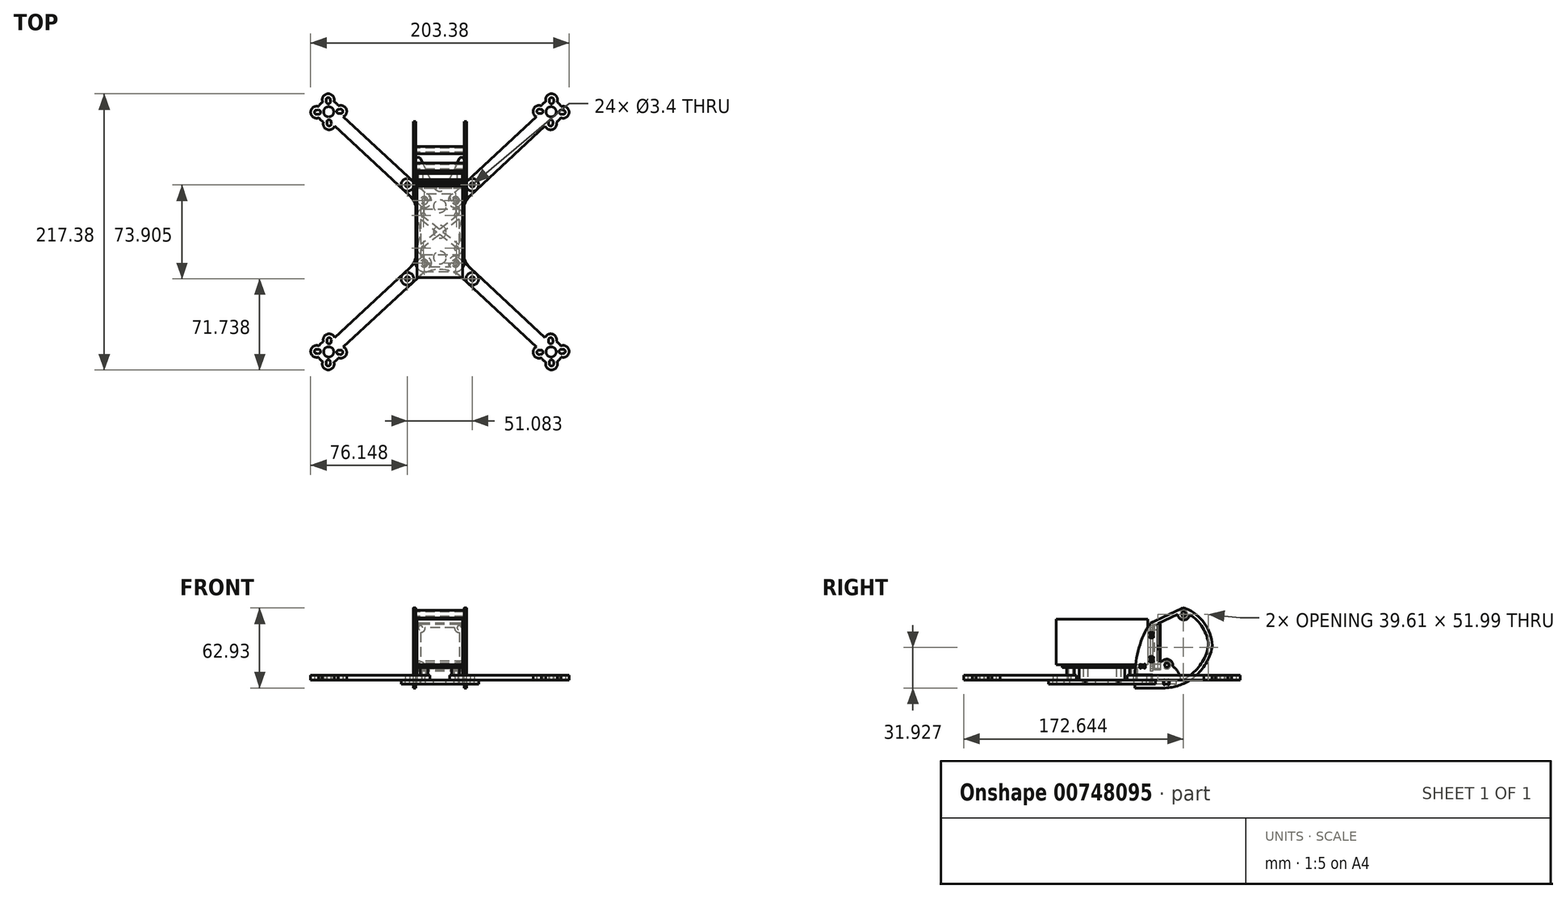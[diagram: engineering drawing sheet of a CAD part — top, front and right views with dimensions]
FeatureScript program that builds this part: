
annotation { "Feature Type Name" : "Feature", "Feature Type Description" : "" }
export const myFeature = defineFeature(function(context is Context, id is Id, definition is map)
    precondition{}
    {
        {
            var Q0;
            Q0=qCreatedBy(makeId("Top.planeOp"),FACE);
            var sketch = newSketch(context, id + "F0", { "sketchPlane" : qUnion([Q0])});
            skCircle(sketch, "E0", {"center": v(-87.5, 94.5) * mm, "radius": 63.5 * mm});
            skCircle(sketch, "E1", {"center": v(87.5, 94.5) * mm, "radius": 63.5 * mm});
            skCircle(sketch, "E2", {"center": v(87.5, -94.5) * mm, "radius": 63.5 * mm});
            skCircle(sketch, "E3", {"center": v(-87.5, -94.5) * mm, "radius": 63.5 * mm});
            skLineSegment(sketch, "E4", {"start": v(-87.5, 94.5) * mm, "end": v(87.5, 94.5) * mm, "construction": true});
            skLineSegment(sketch, "E5", {"start": v(-87.5, 94.5) * mm, "end": v(-87.5, -94.5) * mm, "construction": true});
            skSolve(sketch);
        }
        {
            var Q0;
            Q0=qCreatedBy(makeId("Right.planeOp"),FACE);
            var sketch = newSketch(context, id + "F1", { "sketchPlane" : qUnion([Q0])});
            skLineSegment(sketch, "E6.bottom", {"start": v(36, 41) * mm, "end": v(-36, 41) * mm});
            skLineSegment(sketch, "E6.top", {"start": v(36, 5) * mm, "end": v(-36, 5) * mm});
            skLineSegment(sketch, "E6.left", {"start": v(36, 41) * mm, "end": v(36, 5) * mm});
            skLineSegment(sketch, "E6.right", {"start": v(-36, 41) * mm, "end": v(-36, 5) * mm});
            skSolve(sketch);
        }
        {
            var Q0;
            Q0 = qSketchRegion(id + "F1", true);
            extrude(context, id + "F2", {"entities" : qUnion([Q0]), "endBound" : BoundingType.SYMMETRIC, "depth" : 36 * mm, "offsetDistance" : 25 * mm});
        }
        {
            var Q0;
            Q0=makeQuery(id+"F2.opExtrude","SWEPT_FACE",FACE,{"disambiguationData":[OSD([sQuery(id+"F1.wireOp",EDGE,"E6.left")])]});
            cPlane(context, id + "F3", {"entities" : qUnion([Q0]), "cplaneType" : CPlaneType.OFFSET, "offset" : 2 * mm, "width" : 150 * mm, "height" : 150 * mm});
        }
        {
            var Q0;
            Q0=qCreatedBy(id+"F3.planeOp",FACE);
            var sketch = newSketch(context, id + "F4", { "sketchPlane" : qUnion([Q0])});
            skCircle(sketch, "E7", {"center": v(-15.25, 34.25) * mm, "radius": 1.7 * mm});
            skCircle(sketch, "E8", {"center": v(15.25, 34.25) * mm, "radius": 1.7 * mm});
            skCircle(sketch, "E9", {"center": v(15.25, 3.75) * mm, "radius": 1.7 * mm});
            skCircle(sketch, "E10", {"center": v(-15.25, 3.75) * mm, "radius": 1.7 * mm});
            skLineSegment(sketch, "E11.bottom", {"start": v(-15.25, 37) * mm, "end": v(15.25, 37) * mm, "construction": true});
            skLineSegment(sketch, "E11.top", {"start": v(-15.25, 1) * mm, "end": v(15.25, 1) * mm, "construction": true});
            skLineSegment(sketch, "E11.left", {"start": v(-18, 34.25) * mm, "end": v(-18, 3.75) * mm, "construction": true});
            skLineSegment(sketch, "E11.right", {"start": v(18, 34.25) * mm, "end": v(18, 3.75) * mm, "construction": true});
            skPoint(sketch, "E12.visualSharp", {"position": v(-18, 37) * mm});
            skArc(sketch, "E12.filletArc", {"start": v(-15.25, 37) * mm, "mid": v(-17.2, 36.2) * mm, "end": v(-18, 34.25) * mm, "construction": true});
            skPoint(sketch, "E13.visualSharp", {"position": v(18, 37) * mm});
            skArc(sketch, "E13.filletArc", {"start": v(18, 34.25) * mm, "mid": v(17.2, 36.2) * mm, "end": v(15.25, 37) * mm, "construction": true});
            skPoint(sketch, "E14.visualSharp", {"position": v(18, 1) * mm});
            skArc(sketch, "E14.filletArc", {"start": v(15.25, 1) * mm, "mid": v(17.2, 1.8) * mm, "end": v(18, 3.75) * mm, "construction": true});
            skPoint(sketch, "E15.visualSharp", {"position": v(-18, 1) * mm});
            skArc(sketch, "E15.filletArc", {"start": v(-18, 3.75) * mm, "mid": v(-17.2, 1.8) * mm, "end": v(-15.25, 1) * mm, "construction": true});
            skLineSegment(sketch, "E16.left", {"start": v(-19, 34.25) * mm, "end": v(-19, 31.55) * mm});
            skLineSegment(sketch, "E16.right", {"start": v(19, 34.25) * mm, "end": v(19, 31.55) * mm});
            skLineSegment(sketch, "E17.trimOffspring", {"start": v(-15.25, 0) * mm, "end": v(15.25, 0) * mm});
            skLineSegment(sketch, "E18.trimOffspring", {"start": v(-15.25, 38) * mm, "end": v(15.25, 38) * mm});
            skLineSegment(sketch, "E19.right", {"start": v(15.25, 30.55) * mm, "end": v(15.25, 7.45) * mm});
            skArc(sketch, "E20", {"start": v(-11.55, 34.25) * mm, "mid": v(-12.63, 31.63) * mm, "end": v(-15.25, 30.55) * mm});
            skArc(sketch, "E21", {"start": v(11.55, 34.25) * mm, "mid": v(12.63, 31.63) * mm, "end": v(15.25, 30.55) * mm});
            skArc(sketch, "E22", {"start": v(15.25, 7.45) * mm, "mid": v(12.63, 6.37) * mm, "end": v(11.55, 3.75) * mm});
            skArc(sketch, "E23", {"start": v(-15.25, 7.45) * mm, "mid": v(-12.63, 6.37) * mm, "end": v(-11.55, 3.75) * mm});
            skLineSegment(sketch, "E24.trimOffspring", {"start": v(-11.55, 34.25) * mm, "end": v(11.55, 34.25) * mm});
            skLineSegment(sketch, "E25.trimOffspring", {"start": v(-15.25, 30.55) * mm, "end": v(-15.25, 7.45) * mm});
            skLineSegment(sketch, "E26.trimOffspring", {"start": v(-11.55, 3.75) * mm, "end": v(11.55, 3.75) * mm});
            skArc(sketch, "E27.filletArc", {"start": v(-15.25, 38) * mm, "mid": v(-17.9, 36.9) * mm, "end": v(-19, 34.25) * mm});
            skArc(sketch, "E28.filletArc", {"start": v(19, 34.25) * mm, "mid": v(17.9, 36.9) * mm, "end": v(15.25, 38) * mm});
            skArc(sketch, "E29.filletArc", {"start": v(15.25, 0) * mm, "mid": v(17.9, 1.1) * mm, "end": v(19, 3.75) * mm});
            skArc(sketch, "E30.filletArc", {"start": v(-19, 3.75) * mm, "mid": v(-17.9, 1.1) * mm, "end": v(-15.25, 0) * mm});
            skLineSegment(sketch, "E31.bottom", {"start": v(19, 30.55) * mm, "end": v(21, 30.55) * mm});
            skLineSegment(sketch, "E31.top", {"start": v(19, 26.55) * mm, "end": v(21, 26.55) * mm});
            skLineSegment(sketch, "E31.right", {"start": v(21, 30.55) * mm, "end": v(21, 26.55) * mm});
            skLineSegment(sketch, "E32.bottom", {"start": v(19, 11.45) * mm, "end": v(21, 11.45) * mm});
            skLineSegment(sketch, "E32.top", {"start": v(19, 7.45) * mm, "end": v(21, 7.45) * mm});
            skLineSegment(sketch, "E32.right", {"start": v(21, 11.45) * mm, "end": v(21, 7.45) * mm});
            skLineSegment(sketch, "E33.bottom", {"start": v(-19, 11.45) * mm, "end": v(-21, 11.45) * mm});
            skLineSegment(sketch, "E33.top", {"start": v(-19, 7.45) * mm, "end": v(-21, 7.45) * mm});
            skLineSegment(sketch, "E33.right", {"start": v(-21, 11.45) * mm, "end": v(-21, 7.45) * mm});
            skLineSegment(sketch, "E34.bottom", {"start": v(-19, 26.55) * mm, "end": v(-21, 26.55) * mm});
            skLineSegment(sketch, "E34.top", {"start": v(-19, 30.55) * mm, "end": v(-21, 30.55) * mm});
            skLineSegment(sketch, "E34.right", {"start": v(-21, 26.55) * mm, "end": v(-21, 30.55) * mm});
            skArc(sketch, "E35", {"start": v(-19, 30.55) * mm, "mid": v(-18.5, 31.05) * mm, "end": v(-19, 31.55) * mm});
            skArc(sketch, "E36", {"start": v(-19, 26.55) * mm, "mid": v(-18.5, 26.05) * mm, "end": v(-19, 25.55) * mm});
            skArc(sketch, "E37", {"start": v(19, 30.55) * mm, "mid": v(18.5, 31.05) * mm, "end": v(19, 31.55) * mm});
            skArc(sketch, "E38", {"start": v(19, 26.55) * mm, "mid": v(18.5, 26.05) * mm, "end": v(19, 25.55) * mm});
            skLineSegment(sketch, "E39.trimOffspring", {"start": v(-19, 25.55) * mm, "end": v(-19, 12.45) * mm});
            skLineSegment(sketch, "E40.trimOffspring", {"start": v(19, 25.55) * mm, "end": v(19, 12.45) * mm});
            skArc(sketch, "E41", {"start": v(-19, 11.45) * mm, "mid": v(-18.5, 11.95) * mm, "end": v(-19, 12.45) * mm});
            skArc(sketch, "E42", {"start": v(-19, 7.45) * mm, "mid": v(-18.5, 6.95) * mm, "end": v(-19, 6.45) * mm});
            skLineSegment(sketch, "E43.trimOffspring", {"start": v(-19, 6.45) * mm, "end": v(-19, 3.75) * mm});
            skArc(sketch, "E44", {"start": v(19, 11.45) * mm, "mid": v(18.5, 11.95) * mm, "end": v(19, 12.45) * mm});
            skArc(sketch, "E45", {"start": v(19, 7.45) * mm, "mid": v(18.5, 6.95) * mm, "end": v(19, 6.45) * mm});
            skLineSegment(sketch, "E46.trimOffspring", {"start": v(19, 6.45) * mm, "end": v(19, 3.75) * mm});
            skSolve(sketch);
        }
        {
            var Q0;
            Q0 = qSketchRegion(id + "F4", true);
            extrude(context, id + "F5", {"entities" : qUnion([Q0]), "depth" : 2 * mm, "offsetDistance" : 25 * mm});
        }
        {
            var Q0;
            Q0=makeQuery(id+"F5.opExtrude","CAP_FACE",FACE,{"disambiguationData":[OSD([sQuery(id+"F4.wireOp",EDGE,"E7"),sQuery(id+"F4.wireOp",EDGE,"E8"),sQuery(id+"F4.wireOp",EDGE,"E9"),sQuery(id+"F4.wireOp",EDGE,"E10"),sQuery(id+"F4.wireOp",EDGE,"E16.bottom"),sQuery(id+"F4.wireOp",EDGE,"E16.top"),sQuery(id+"F4.wireOp",EDGE,"E16.left"),sQuery(id+"F4.wireOp",EDGE,"E16.right"),sQuery(id+"F4.wireOp",EDGE,"0tjX9AGm-dfaZ-di7K-9Cjz-SUyM1mQiOhD7.top"),sQuery(id+"F4.wireOp",EDGE,"0tjX9AGm-dfaZ-di7K-9Cjz-SUyM1mQiOhD7.left"),sQuery(id+"F4.wireOp",EDGE,"0tjX9AGm-dfaZ-di7K-9Cjz-SUyM1mQiOhD7.right"),sQuery(id+"F4.wireOp",EDGE,"jNbVTTfh-dDnQ-iOIQ-lGc2-BmaGoyWdqRNK.top"),sQuery(id+"F4.wireOp",EDGE,"jNbVTTfh-dDnQ-iOIQ-lGc2-BmaGoyWdqRNK.left"),sQuery(id+"F4.wireOp",EDGE,"jNbVTTfh-dDnQ-iOIQ-lGc2-BmaGoyWdqRNK.right"),sQuery(id+"F4.wireOp",EDGE,"p8So4zwG-Bp0h-plD2-JnCm-BeE0CadOh8gG.top"),sQuery(id+"F4.wireOp",EDGE,"p8So4zwG-Bp0h-plD2-JnCm-BeE0CadOh8gG.left"),sQuery(id+"F4.wireOp",EDGE,"p8So4zwG-Bp0h-plD2-JnCm-BeE0CadOh8gG.right"),sQuery(id+"F4.wireOp",EDGE,"Rqj2pUDk-Wo8M-VqOy-AQv9-rM1yGNZkRYXT.top"),sQuery(id+"F4.wireOp",EDGE,"Rqj2pUDk-Wo8M-VqOy-AQv9-rM1yGNZkRYXT.left"),sQuery(id+"F4.wireOp",EDGE,"Rqj2pUDk-Wo8M-VqOy-AQv9-rM1yGNZkRYXT.right"),sQuery(id+"F4.wireOp",EDGE,"cf8581b7-b0b2-420e-8d79-318895d83493.trimOffspring"),sQuery(id+"F4.wireOp",EDGE,"E17.trimOffspring"),sQuery(id+"F4.wireOp",EDGE,"E18.trimOffspring"),sQuery(id+"F4.wireOp",EDGE,"2b6bb1a9-3bb7-41ad-b322-06cd7e0aa122.trimOffspring"),sQuery(id+"F4.wireOp",EDGE,"E19.right"),sQuery(id+"F4.wireOp",EDGE,"E20"),sQuery(id+"F4.wireOp",EDGE,"E21"),sQuery(id+"F4.wireOp",EDGE,"E22"),sQuery(id+"F4.wireOp",EDGE,"E23"),sQuery(id+"F4.wireOp",EDGE,"E24.trimOffspring"),sQuery(id+"F4.wireOp",EDGE,"E25.trimOffspring"),sQuery(id+"F4.wireOp",EDGE,"E26.trimOffspring"),sQuery(id+"F4.wireOp",EDGE,"E27.filletArc"),sQuery(id+"F4.wireOp",EDGE,"E28.filletArc"),sQuery(id+"F4.wireOp",EDGE,"E29.filletArc"),sQuery(id+"F4.wireOp",EDGE,"E30.filletArc")])],"isStart":false});
            cPlane(context, id + "F6", {"entities" : qUnion([Q0]), "cplaneType" : CPlaneType.OFFSET, "offset" : 1 * mm, "width" : 150 * mm, "height" : 150 * mm});
        }
        {
            var Q0;
            Q0=qCreatedBy(id+"F6.planeOp",FACE);
            var sketch = newSketch(context, id + "F7", { "sketchPlane" : qUnion([Q0])});
            skCircle(sketch, "E47", {"center": v(-15.25, 34.25) * mm, "radius": 1.7 * mm});
            skCircle(sketch, "E48", {"center": v(15.25, 34.25) * mm, "radius": 1.7 * mm});
            skCircle(sketch, "E49", {"center": v(15.25, 3.75) * mm, "radius": 1.7 * mm});
            skCircle(sketch, "E50", {"center": v(-15.25, 3.75) * mm, "radius": 1.7 * mm});
            skLineSegment(sketch, "E51.bottom", {"start": v(-15.25, 37) * mm, "end": v(15.25, 37) * mm});
            skLineSegment(sketch, "E51.top", {"start": v(-15.25, 1) * mm, "end": v(15.25, 1) * mm});
            skLineSegment(sketch, "E51.left", {"start": v(-18, 34.25) * mm, "end": v(-18, 3.75) * mm});
            skLineSegment(sketch, "E51.right", {"start": v(18, 34.25) * mm, "end": v(18, 3.75) * mm});
            skPoint(sketch, "E52.visualSharp", {"position": v(-18, 37) * mm});
            skArc(sketch, "E52.filletArc", {"start": v(-15.25, 37) * mm, "mid": v(-17.2, 36.2) * mm, "end": v(-18, 34.25) * mm});
            skPoint(sketch, "E53.visualSharp", {"position": v(18, 37) * mm});
            skArc(sketch, "E53.filletArc", {"start": v(18, 34.25) * mm, "mid": v(17.2, 36.2) * mm, "end": v(15.25, 37) * mm});
            skPoint(sketch, "E54.visualSharp", {"position": v(18, 1) * mm});
            skArc(sketch, "E54.filletArc", {"start": v(15.25, 1) * mm, "mid": v(17.2, 1.8) * mm, "end": v(18, 3.75) * mm});
            skPoint(sketch, "E55.visualSharp", {"position": v(-18, 1) * mm});
            skArc(sketch, "E55.filletArc", {"start": v(-18, 3.75) * mm, "mid": v(-17.2, 1.8) * mm, "end": v(-15.25, 1) * mm});
            skSolve(sketch);
        }
        {
            var Q0;
            Q0 = qSketchRegion(id + "F7", true);
            extrude(context, id + "F8", {"entities" : qUnion([Q0]), "depth" : 5 * mm, "offsetDistance" : 25 * mm});
        }
        {
            var Q0;
            Q0=qCreatedBy(makeId("Right.planeOp"),FACE);
            cPlane(context, id + "F9", {"entities" : qUnion([Q0]), "cplaneType" : CPlaneType.OFFSET, "offset" : 19 * mm, "oppositeDirection" : true, "width" : 150 * mm, "height" : 150 * mm});
        }
        {
            var Q0;
            Q0=qCreatedBy(makeId("Top.planeOp"),FACE);
            cPlane(context, id + "F10", {"entities" : qUnion([Q0]), "cplaneType" : CPlaneType.OFFSET, "offset" : 3 * mm, "oppositeDirection" : true, "width" : 150 * mm, "height" : 150 * mm});
        }
        {
            var Q0;
            Q0=qCreatedBy(id+"F10.planeOp",FACE);
            var sketch = newSketch(context, id + "F11", { "sketchPlane" : qUnion([Q0])});
            skLineSegment(sketch, "E56.bottom", {"start": v(-22.09, 35.9) * mm, "end": v(22.09, 35.9) * mm});
            skLineSegment(sketch, "E56.top", {"start": v(-22.09, -35.74) * mm, "end": v(22.09, -35.74) * mm});
            skLineSegment(sketch, "E56.left", {"start": v(-22.09, 35.9) * mm, "end": v(-22.09, -35.74) * mm});
            skLineSegment(sketch, "E56.right", {"start": v(22.09, 35.9) * mm, "end": v(22.09, -35.74) * mm});
            skLineSegment(sketch, "E57.bottom", {"start": v(-16.09, 32.9) * mm, "end": v(16.09, 32.9) * mm});
            skLineSegment(sketch, "E57.top", {"start": v(-16.09, -32.74) * mm, "end": v(16.09, -32.74) * mm});
            skLineSegment(sketch, "E57.left", {"start": v(-19.09, 29.9) * mm, "end": v(-19.09, -29.74) * mm});
            skLineSegment(sketch, "E57.right", {"start": v(19.09, 29.9) * mm, "end": v(19.09, -29.74) * mm});
            skPoint(sketch, "E58.visualSharp", {"position": v(-19.09, 32.9) * mm});
            skArc(sketch, "E58.filletArc", {"start": v(-16.09, 32.9) * mm, "mid": v(-18.2, 32.02) * mm, "end": v(-19.09, 29.9) * mm});
            skPoint(sketch, "E59.visualSharp", {"position": v(19.09, 32.9) * mm});
            skArc(sketch, "E59.filletArc", {"start": v(19.09, 29.9) * mm, "mid": v(18.2, 32.02) * mm, "end": v(16.09, 32.9) * mm});
            skPoint(sketch, "E60.visualSharp", {"position": v(19.09, -32.74) * mm});
            skArc(sketch, "E60.filletArc", {"start": v(16.09, -32.74) * mm, "mid": v(18.2, -31.86) * mm, "end": v(19.09, -29.74) * mm});
            skPoint(sketch, "E61.visualSharp", {"position": v(-19.09, -32.74) * mm});
            skArc(sketch, "E61.filletArc", {"start": v(-19.09, -29.74) * mm, "mid": v(-18.2, -31.86) * mm, "end": v(-16.09, -32.74) * mm});
            skLineSegment(sketch, "E62.bottom", {"start": v(-18, 18) * mm, "end": v(18, 18) * mm, "construction": true});
            skLineSegment(sketch, "E62.top", {"start": v(-18, -18) * mm, "end": v(18, -18) * mm, "construction": true});
            skLineSegment(sketch, "E62.left", {"start": v(-18, 18) * mm, "end": v(-18, -18) * mm, "construction": true});
            skLineSegment(sketch, "E62.right", {"start": v(18, 18) * mm, "end": v(18, -18) * mm, "construction": true});
            skCircle(sketch, "E63", {"center": v(-25.54, 36.95) * mm, "radius": 1.7 * mm});
            skCircle(sketch, "E64", {"center": v(25.54, 36.95) * mm, "radius": 1.7 * mm});
            skCircle(sketch, "E65", {"center": v(-25.54, -36.95) * mm, "radius": 1.7 * mm});
            skCircle(sketch, "E66", {"center": v(25.54, -36.95) * mm, "radius": 1.7 * mm});
            skLineSegment(sketch, "E67", {"start": v(-87.5, 94.5) * mm, "end": v(-12.35, 24.7) * mm, "construction": true});
            skCircle(sketch, "E68.cCircle", {"center": v(-25.54, 36.95) * mm, "radius": 2.6 * mm, "construction": true});
            skLineSegment(sketch, "E68.0", {"start": v(-27.04, 39.55) * mm, "end": v(-24.04, 39.55) * mm, "construction": true});
            skLineSegment(sketch, "E68.1", {"start": v(-24.04, 39.55) * mm, "end": v(-22.54, 36.95) * mm, "construction": true});
            skLineSegment(sketch, "E68.2", {"start": v(-22.54, 36.95) * mm, "end": v(-24.04, 34.35) * mm, "construction": true});
            skLineSegment(sketch, "E68.3", {"start": v(-24.04, 34.35) * mm, "end": v(-27.04, 34.35) * mm, "construction": true});
            skLineSegment(sketch, "E68.4", {"start": v(-27.04, 34.35) * mm, "end": v(-28.54, 36.95) * mm, "construction": true});
            skLineSegment(sketch, "E68.5", {"start": v(-28.54, 36.95) * mm, "end": v(-27.04, 39.55) * mm, "construction": true});
            skPoint(sketch, "E68.0.midPoint", {"position": v(-25.54, 39.55) * mm});
            skCircle(sketch, "E69", {"center": v(-12.35, 24.7) * mm, "radius": 1.7 * mm, "construction": true});
            skCircle(sketch, "E70.cCircle", {"center": v(-12.35, 24.7) * mm, "radius": 2.6 * mm, "construction": true});
            skLineSegment(sketch, "E70.0", {"start": v(-12.35, 27.7) * mm, "end": v(-9.75, 26.2) * mm});
            skLineSegment(sketch, "E70.1", {"start": v(-9.75, 26.2) * mm, "end": v(-9.75, 23.2) * mm});
            skLineSegment(sketch, "E70.2", {"start": v(-9.75, 23.2) * mm, "end": v(-12.35, 21.7) * mm});
            skLineSegment(sketch, "E70.3", {"start": v(-12.35, 21.7) * mm, "end": v(-14.95, 23.2) * mm});
            skLineSegment(sketch, "E70.4", {"start": v(-14.95, 23.2) * mm, "end": v(-14.95, 26.2) * mm});
            skLineSegment(sketch, "E70.5", {"start": v(-14.95, 26.2) * mm, "end": v(-12.35, 27.7) * mm});
            skPoint(sketch, "E70.0.midPoint", {"position": v(-11.05, 26.95) * mm});
            skSolve(sketch);
        }
        {
            var Q0;
            Q0=qCreatedBy(id+"F10.planeOp",FACE);
            cPlane(context, id + "F12", {"entities" : qUnion([Q0]), "cplaneType" : CPlaneType.OFFSET, "offset" : 4 * mm, "oppositeDirection" : true, "width" : 150 * mm, "height" : 150 * mm});
        }
        {
            var Q0;
            Q0=qCreatedBy(id+"F12.planeOp",FACE);
            var sketch = newSketch(context, id + "F13", { "sketchPlane" : qUnion([Q0])});
            skCircle(sketch, "E71", {"center": v(-25.54, 36.95) * mm, "radius": 1.7 * mm});
            skArc(sketch, "E72", {"start": v(-11.2, 25.95) * mm, "mid": v(-13.6, 25.86) * mm, "end": v(-13.5, 23.46) * mm});
            skLineSegment(sketch, "E73", {"start": v(-75.97, 90.61) * mm, "end": v(-7.83, 27.33) * mm});
            skLineSegment(sketch, "E74", {"start": v(-14.64, 20) * mm, "end": v(-82.78, 83.29) * mm});
            skLineSegment(sketch, "E75", {"start": v(-11.2, 25.95) * mm, "end": v(-9.95, 24.8) * mm});
            skLineSegment(sketch, "E76", {"start": v(-13.5, 23.46) * mm, "end": v(-12.26, 22.3) * mm});
            skLineSegment(sketch, "E77", {"start": v(-7.83, 27.33) * mm, "end": v(-8.3, 25.3) * mm});
            skLineSegment(sketch, "E78", {"start": v(-12.65, 20.61) * mm, "end": v(-14.64, 20) * mm});
            skPoint(sketch, "E79.visualSharp", {"position": v(-11, 21.12) * mm});
            skArc(sketch, "E79.filletArc", {"start": v(-12.65, 20.61) * mm, "mid": v(-11.97, 21.34) * mm, "end": v(-12.26, 22.3) * mm});
            skPoint(sketch, "E80.visualSharp", {"position": v(-8.68, 23.61) * mm});
            skArc(sketch, "E80.filletArc", {"start": v(-9.95, 24.8) * mm, "mid": v(-8.98, 24.57) * mm, "end": v(-8.3, 25.3) * mm});
            skCircle(sketch, "E81", {"center": v(-87.5, 94.5) * mm, "radius": 4 * mm});
            skArc(sketch, "E82", {"start": v(-88.85, 84.94) * mm, "mid": v(-87.09, 83.3) * mm, "end": v(-85.45, 85.07) * mm});
            skLineSegment(sketch, "E83", {"start": v(-87.15, 85) * mm, "end": v(-87.85, 104) * mm, "construction": true});
            skLineSegment(sketch, "E84", {"start": v(-89.55, 103.93) * mm, "end": v(-89.5, 102.43) * mm});
            skLineSegment(sketch, "E85.trimOffspring", {"start": v(-85.5, 86.57) * mm, "end": v(-85.45, 85.07) * mm});
            skLineSegment(sketch, "E86.trimOffspring", {"start": v(-88.9, 86.44) * mm, "end": v(-88.85, 84.94) * mm});
            skLineSegment(sketch, "E87", {"start": v(-86.1, 102.56) * mm, "end": v(-86.15, 104.06) * mm});
            skLineSegment(sketch, "E88", {"start": v(-97.06, 95.85) * mm, "end": v(-95.56, 95.9) * mm});
            skLineSegment(sketch, "E89", {"start": v(-77.94, 93.15) * mm, "end": v(-79.44, 93.1) * mm});
            skLineSegment(sketch, "E90.trimOffspring", {"start": v(-95.43, 92.5) * mm, "end": v(-96.93, 92.45) * mm});
            skLineSegment(sketch, "E91.trimOffspring", {"start": v(-79.57, 96.5) * mm, "end": v(-78.07, 96.55) * mm});
            skLineSegment(sketch, "E92", {"start": v(-97, 94.15) * mm, "end": v(-78, 94.85) * mm, "construction": true});
            skArc(sketch, "E93", {"start": v(-95.5, 98.6) * mm, "mid": v(-101.7, 93.98) * mm, "end": v(-95.17, 89.82) * mm});
            skArc(sketch, "E94", {"start": v(-92.18, 102.17) * mm, "mid": v(-88.02, 108.7) * mm, "end": v(-83.4, 102.5) * mm});
            skArc(sketch, "E95", {"start": v(-79.83, 99.18) * mm, "mid": v(-73.3, 95.02) * mm, "end": v(-79.5, 90.4) * mm});
            skArc(sketch, "E96", {"start": v(-91.6, 86.5) * mm, "mid": v(-86.98, 80.3) * mm, "end": v(-82.82, 86.83) * mm});
            skArc(sketch, "E97.trimOffspring", {"start": v(-95.17, 89.82) * mm, "mid": v(-93.62, 87.92) * mm, "end": v(-91.6, 86.5) * mm});
            skArc(sketch, "E98.trimOffspring", {"start": v(-95.43, 92.5) * mm, "mid": v(-93.8, 94.27) * mm, "end": v(-95.56, 95.9) * mm});
            skArc(sketch, "E99.trimOffspring", {"start": v(-97.06, 95.85) * mm, "mid": v(-98.7, 94.09) * mm, "end": v(-96.93, 92.45) * mm});
            skArc(sketch, "E100.trimOffspring", {"start": v(-89.5, 102.43) * mm, "mid": v(-87.73, 100.8) * mm, "end": v(-86.1, 102.56) * mm});
            skArc(sketch, "E101.trimOffspring", {"start": v(-86.15, 104.06) * mm, "mid": v(-87.91, 105.7) * mm, "end": v(-89.55, 103.93) * mm});
            skArc(sketch, "E102.trimOffspring", {"start": v(-92.18, 102.17) * mm, "mid": v(-94.08, 100.62) * mm, "end": v(-95.5, 98.6) * mm});
            skArc(sketch, "E103.trimOffspring", {"start": v(-79.83, 99.18) * mm, "mid": v(-81.38, 101.08) * mm, "end": v(-83.4, 102.5) * mm});
            skArc(sketch, "E104.trimOffspring", {"start": v(-77.94, 93.15) * mm, "mid": v(-76.3, 94.91) * mm, "end": v(-78.07, 96.55) * mm});
            skArc(sketch, "E105.trimOffspring", {"start": v(-79.57, 96.5) * mm, "mid": v(-81.2, 94.73) * mm, "end": v(-79.44, 93.1) * mm});
            skArc(sketch, "E106.trimOffspring", {"start": v(-82.82, 86.83) * mm, "mid": v(-80.92, 88.38) * mm, "end": v(-79.5, 90.4) * mm});
            skArc(sketch, "E107.trimOffspring", {"start": v(-85.5, 86.57) * mm, "mid": v(-87.27, 88.2) * mm, "end": v(-88.9, 86.44) * mm});
            skLineSegment(sketch, "E108", {"start": v(-12.35, 24.7) * mm, "end": v(-87.5, 94.5) * mm, "construction": true});
            skArc(sketch, "E109.MirrorCS", {"start": v(86.15, 104.06) * mm, "mid": v(87.91, 105.7) * mm, "end": v(89.55, 103.93) * mm});
            skLineSegment(sketch, "E110.MirrorCS", {"start": v(79.57, 96.5) * mm, "end": v(78.07, 96.55) * mm});
            skArc(sketch, "E111.MirrorCS", {"start": v(79.57, 96.5) * mm, "mid": v(81.2, 94.73) * mm, "end": v(79.44, 93.1) * mm});
            skLineSegment(sketch, "E112.MirrorCS", {"start": v(7.83, 27.33) * mm, "end": v(8.3, 25.3) * mm});
            skLineSegment(sketch, "E113.MirrorCS", {"start": v(86.1, 102.56) * mm, "end": v(86.15, 104.06) * mm});
            skArc(sketch, "E114.MirrorCS", {"start": v(88.85, 84.94) * mm, "mid": v(87.09, 83.3) * mm, "end": v(85.45, 85.07) * mm});
            skLineSegment(sketch, "E115.MirrorCS", {"start": v(97.06, 95.85) * mm, "end": v(95.56, 95.9) * mm});
            skArc(sketch, "E116.MirrorCS", {"start": v(89.5, 102.43) * mm, "mid": v(87.73, 100.8) * mm, "end": v(86.1, 102.56) * mm});
            skArc(sketch, "E117.MirrorCS", {"start": v(97.06, 95.85) * mm, "mid": v(98.7, 94.09) * mm, "end": v(96.93, 92.45) * mm});
            skLineSegment(sketch, "E118.MirrorCS", {"start": v(12.65, 20.61) * mm, "end": v(14.64, 20) * mm});
            skLineSegment(sketch, "E119.MirrorCS", {"start": v(89.55, 103.93) * mm, "end": v(89.5, 102.43) * mm});
            skLineSegment(sketch, "E120.MirrorCS", {"start": v(95.43, 92.5) * mm, "end": v(96.93, 92.45) * mm});
            skArc(sketch, "E121.MirrorCS", {"start": v(12.65, 20.61) * mm, "mid": v(11.97, 21.34) * mm, "end": v(12.26, 22.3) * mm});
            skLineSegment(sketch, "E122.MirrorCS", {"start": v(77.94, 93.15) * mm, "end": v(79.44, 93.1) * mm});
            skLineSegment(sketch, "E123.MirrorCS", {"start": v(85.5, 86.57) * mm, "end": v(85.45, 85.07) * mm});
            skArc(sketch, "E124.MirrorCS", {"start": v(9.95, 24.8) * mm, "mid": v(8.98, 24.57) * mm, "end": v(8.3, 25.3) * mm});
            skLineSegment(sketch, "E125.MirrorCS", {"start": v(88.9, 86.44) * mm, "end": v(88.85, 84.94) * mm});
            skLineSegment(sketch, "E126.MirrorCS", {"start": v(13.5, 23.46) * mm, "end": v(12.26, 22.3) * mm});
            skArc(sketch, "E127.MirrorCS", {"start": v(95.43, 92.5) * mm, "mid": v(93.8, 94.27) * mm, "end": v(95.56, 95.9) * mm});
            skLineSegment(sketch, "E128.MirrorCS", {"start": v(11.2, 25.95) * mm, "end": v(9.95, 24.8) * mm});
            skArc(sketch, "E129.MirrorCS", {"start": v(77.94, 93.15) * mm, "mid": v(76.3, 94.91) * mm, "end": v(78.07, 96.55) * mm});
            skArc(sketch, "E130.MirrorCS", {"start": v(11.2, 25.95) * mm, "mid": v(13.6, 25.86) * mm, "end": v(13.5, 23.46) * mm});
            skArc(sketch, "E131.MirrorCS", {"start": v(85.5, 86.57) * mm, "mid": v(87.27, 88.2) * mm, "end": v(88.9, 86.44) * mm});
            skArc(sketch, "E132.MirrorCS", {"start": v(82.82, 86.83) * mm, "mid": v(80.92, 88.38) * mm, "end": v(79.5, 90.4) * mm});
            skLineSegment(sketch, "E133.MirrorCS", {"start": v(87.15, 85) * mm, "end": v(87.85, 104) * mm, "construction": true});
            skArc(sketch, "E134.MirrorCS", {"start": v(79.83, 99.18) * mm, "mid": v(81.38, 101.08) * mm, "end": v(83.4, 102.5) * mm});
            skArc(sketch, "E135.MirrorCS", {"start": v(95.17, 89.82) * mm, "mid": v(93.62, 87.92) * mm, "end": v(91.6, 86.5) * mm});
            skArc(sketch, "E136.MirrorCS", {"start": v(92.18, 102.17) * mm, "mid": v(94.08, 100.62) * mm, "end": v(95.5, 98.6) * mm});
            skLineSegment(sketch, "E137.MirrorCS", {"start": v(12.35, 24.7) * mm, "end": v(87.5, 94.5) * mm, "construction": true});
            skLineSegment(sketch, "E138.MirrorCS", {"start": v(97, 94.15) * mm, "end": v(78, 94.85) * mm, "construction": true});
            skArc(sketch, "E139.MirrorCS", {"start": v(91.6, 86.5) * mm, "mid": v(86.98, 80.3) * mm, "end": v(82.82, 86.83) * mm});
            skCircle(sketch, "E140.MirrorC", {"center": v(25.54, 36.95) * mm, "radius": 1.7 * mm});
            skCircle(sketch, "E141.MirrorC", {"center": v(87.5, 94.5) * mm, "radius": 4 * mm});
            skLineSegment(sketch, "E142.MirrorCS", {"start": v(75.97, 90.61) * mm, "end": v(7.83, 27.33) * mm});
            skLineSegment(sketch, "E143.MirrorCS", {"start": v(14.64, 20) * mm, "end": v(82.78, 83.29) * mm});
            skArc(sketch, "E144.MirrorCS", {"start": v(92.18, 102.17) * mm, "mid": v(88.02, 108.7) * mm, "end": v(83.4, 102.5) * mm});
            skArc(sketch, "E145.MirrorCS", {"start": v(79.83, 99.18) * mm, "mid": v(73.3, 95.02) * mm, "end": v(79.5, 90.4) * mm});
            skPoint(sketch, "E146.MirrorP", {"position": v(11, 21.12) * mm});
            skArc(sketch, "E147.MirrorCS", {"start": v(95.5, 98.6) * mm, "mid": v(101.7, 93.98) * mm, "end": v(95.17, 89.82) * mm});
            skPoint(sketch, "E148.MirrorP", {"position": v(8.68, 23.61) * mm});
            skLineSegment(sketch, "E149.MirrorCS", {"start": v(95.43, -92.5) * mm, "end": v(96.93, -92.45) * mm});
            skArc(sketch, "E150.MirrorCS", {"start": v(97.06, -95.85) * mm, "mid": v(98.7, -94.09) * mm, "end": v(96.93, -92.45) * mm});
            skLineSegment(sketch, "E151.MirrorCS", {"start": v(97.06, -95.85) * mm, "end": v(95.56, -95.9) * mm});
            skLineSegment(sketch, "E152.MirrorCS", {"start": v(88.9, -86.44) * mm, "end": v(88.85, -84.94) * mm});
            skLineSegment(sketch, "E153.MirrorCS", {"start": v(11.2, -25.95) * mm, "end": v(9.95, -24.8) * mm});
            skLineSegment(sketch, "E154.MirrorCS", {"start": v(7.83, -27.33) * mm, "end": v(8.3, -25.3) * mm});
            skArc(sketch, "E155.MirrorCS", {"start": v(9.95, -24.8) * mm, "mid": v(8.98, -24.57) * mm, "end": v(8.3, -25.3) * mm});
            skArc(sketch, "E156.MirrorCS", {"start": v(88.85, -84.94) * mm, "mid": v(87.09, -83.3) * mm, "end": v(85.45, -85.07) * mm});
            skLineSegment(sketch, "E157.MirrorCS", {"start": v(-11.2, -25.95) * mm, "end": v(-9.95, -24.8) * mm});
            skLineSegment(sketch, "E158.MirrorCS", {"start": v(-88.9, -86.44) * mm, "end": v(-88.85, -84.94) * mm});
            skArc(sketch, "E159.MirrorCS", {"start": v(-77.94, -93.15) * mm, "mid": v(-76.3, -94.91) * mm, "end": v(-78.07, -96.55) * mm});
            skLineSegment(sketch, "E160.MirrorCS", {"start": v(85.5, -86.57) * mm, "end": v(85.45, -85.07) * mm});
            skLineSegment(sketch, "E161.MirrorCS", {"start": v(-7.83, -27.33) * mm, "end": v(-8.3, -25.3) * mm});
            skArc(sketch, "E162.MirrorCS", {"start": v(-9.95, -24.8) * mm, "mid": v(-8.98, -24.57) * mm, "end": v(-8.3, -25.3) * mm});
            skLineSegment(sketch, "E163.MirrorCS", {"start": v(-85.5, -86.57) * mm, "end": v(-85.45, -85.07) * mm});
            skArc(sketch, "E164.MirrorCS", {"start": v(-88.85, -84.94) * mm, "mid": v(-87.09, -83.3) * mm, "end": v(-85.45, -85.07) * mm});
            skLineSegment(sketch, "E165.MirrorCS", {"start": v(-77.94, -93.15) * mm, "end": v(-79.44, -93.1) * mm});
            skLineSegment(sketch, "E166.MirrorCS", {"start": v(-79.57, -96.5) * mm, "end": v(-78.07, -96.55) * mm});
            skLineSegment(sketch, "E167.MirrorCS", {"start": v(-13.5, -23.46) * mm, "end": v(-12.26, -22.3) * mm});
            skArc(sketch, "E168.MirrorCS", {"start": v(-12.65, -20.61) * mm, "mid": v(-11.97, -21.34) * mm, "end": v(-12.26, -22.3) * mm});
            skLineSegment(sketch, "E169.MirrorCS", {"start": v(89.55, -103.93) * mm, "end": v(89.5, -102.43) * mm});
            skLineSegment(sketch, "E170.MirrorCS", {"start": v(-12.65, -20.61) * mm, "end": v(-14.64, -20) * mm});
            skLineSegment(sketch, "E171.MirrorCS", {"start": v(86.1, -102.56) * mm, "end": v(86.15, -104.06) * mm});
            skArc(sketch, "E172.MirrorCS", {"start": v(89.5, -102.43) * mm, "mid": v(87.73, -100.8) * mm, "end": v(86.1, -102.56) * mm});
            skArc(sketch, "E173.MirrorCS", {"start": v(79.57, -96.5) * mm, "mid": v(81.2, -94.73) * mm, "end": v(79.44, -93.1) * mm});
            skLineSegment(sketch, "E174.MirrorCS", {"start": v(13.5, -23.46) * mm, "end": v(12.26, -22.3) * mm});
            skLineSegment(sketch, "E175.MirrorCS", {"start": v(-95.43, -92.5) * mm, "end": v(-96.93, -92.45) * mm});
            skLineSegment(sketch, "E176.MirrorCS", {"start": v(12.65, -20.61) * mm, "end": v(14.64, -20) * mm});
            skArc(sketch, "E177.MirrorCS", {"start": v(95.43, -92.5) * mm, "mid": v(93.8, -94.27) * mm, "end": v(95.56, -95.9) * mm});
            skArc(sketch, "E178.MirrorCS", {"start": v(-97.06, -95.85) * mm, "mid": v(-98.7, -94.09) * mm, "end": v(-96.93, -92.45) * mm});
            skArc(sketch, "E179.MirrorCS", {"start": v(12.65, -20.61) * mm, "mid": v(11.97, -21.34) * mm, "end": v(12.26, -22.3) * mm});
            skLineSegment(sketch, "E180.MirrorCS", {"start": v(79.57, -96.5) * mm, "end": v(78.07, -96.55) * mm});
            skLineSegment(sketch, "E181.MirrorCS", {"start": v(-97.06, -95.85) * mm, "end": v(-95.56, -95.9) * mm});
            skArc(sketch, "E182.MirrorCS", {"start": v(-79.57, -96.5) * mm, "mid": v(-81.2, -94.73) * mm, "end": v(-79.44, -93.1) * mm});
            skArc(sketch, "E183.MirrorCS", {"start": v(86.15, -104.06) * mm, "mid": v(87.91, -105.7) * mm, "end": v(89.55, -103.93) * mm});
            skArc(sketch, "E184.MirrorCS", {"start": v(77.94, -93.15) * mm, "mid": v(76.3, -94.91) * mm, "end": v(78.07, -96.55) * mm});
            skArc(sketch, "E185.MirrorCS", {"start": v(-95.43, -92.5) * mm, "mid": v(-93.8, -94.27) * mm, "end": v(-95.56, -95.9) * mm});
            skArc(sketch, "E186.MirrorCS", {"start": v(-85.5, -86.57) * mm, "mid": v(-87.27, -88.2) * mm, "end": v(-88.9, -86.44) * mm});
            skArc(sketch, "E187.MirrorCS", {"start": v(-86.15, -104.06) * mm, "mid": v(-87.91, -105.7) * mm, "end": v(-89.55, -103.93) * mm});
            skArc(sketch, "E188.MirrorCS", {"start": v(82.82, -86.83) * mm, "mid": v(80.92, -88.38) * mm, "end": v(79.5, -90.4) * mm});
            skArc(sketch, "E189.MirrorCS", {"start": v(-89.5, -102.43) * mm, "mid": v(-87.73, -100.8) * mm, "end": v(-86.1, -102.56) * mm});
            skLineSegment(sketch, "E190.MirrorCS", {"start": v(-86.1, -102.56) * mm, "end": v(-86.15, -104.06) * mm});
            skLineSegment(sketch, "E191.MirrorCS", {"start": v(77.94, -93.15) * mm, "end": v(79.44, -93.1) * mm});
            skLineSegment(sketch, "E192.MirrorCS", {"start": v(-89.55, -103.93) * mm, "end": v(-89.5, -102.43) * mm});
            skArc(sketch, "E193.MirrorCS", {"start": v(85.5, -86.57) * mm, "mid": v(87.27, -88.2) * mm, "end": v(88.9, -86.44) * mm});
            skArc(sketch, "E194.MirrorCS", {"start": v(-82.82, -86.83) * mm, "mid": v(-80.92, -88.38) * mm, "end": v(-79.5, -90.4) * mm});
            skArc(sketch, "E195.MirrorCS", {"start": v(-11.2, -25.95) * mm, "mid": v(-13.6, -25.86) * mm, "end": v(-13.5, -23.46) * mm});
            skArc(sketch, "E196.MirrorCS", {"start": v(79.83, -99.18) * mm, "mid": v(81.38, -101.08) * mm, "end": v(83.4, -102.5) * mm});
            skArc(sketch, "E197.MirrorCS", {"start": v(-92.18, -102.17) * mm, "mid": v(-94.08, -100.62) * mm, "end": v(-95.5, -98.6) * mm});
            skLineSegment(sketch, "E198.MirrorCS", {"start": v(-87.15, -85) * mm, "end": v(-87.85, -104) * mm, "construction": true});
            skArc(sketch, "E199.MirrorCS", {"start": v(-79.83, -99.18) * mm, "mid": v(-81.38, -101.08) * mm, "end": v(-83.4, -102.5) * mm});
            skArc(sketch, "E200.MirrorCS", {"start": v(-95.17, -89.82) * mm, "mid": v(-93.62, -87.92) * mm, "end": v(-91.6, -86.5) * mm});
            skLineSegment(sketch, "E201.MirrorCS", {"start": v(87.15, -85) * mm, "end": v(87.85, -104) * mm, "construction": true});
            skArc(sketch, "E202.MirrorCS", {"start": v(95.17, -89.82) * mm, "mid": v(93.62, -87.92) * mm, "end": v(91.6, -86.5) * mm});
            skArc(sketch, "E203.MirrorCS", {"start": v(92.18, -102.17) * mm, "mid": v(94.08, -100.62) * mm, "end": v(95.5, -98.6) * mm});
            skArc(sketch, "E204.MirrorCS", {"start": v(11.2, -25.95) * mm, "mid": v(13.6, -25.86) * mm, "end": v(13.5, -23.46) * mm});
            skLineSegment(sketch, "E205.MirrorCS", {"start": v(97, -94.15) * mm, "end": v(78, -94.85) * mm, "construction": true});
            skLineSegment(sketch, "E206.MirrorCS", {"start": v(-97, -94.15) * mm, "end": v(-78, -94.85) * mm, "construction": true});
            skCircle(sketch, "E207.MirrorC", {"center": v(25.54, -36.95) * mm, "radius": 1.7 * mm});
            skCircle(sketch, "E208.MirrorC", {"center": v(87.5, -94.5) * mm, "radius": 4 * mm});
            skCircle(sketch, "E209.MirrorC", {"center": v(-87.5, -94.5) * mm, "radius": 4 * mm});
            skCircle(sketch, "E210.MirrorC", {"center": v(-25.54, -36.95) * mm, "radius": 1.7 * mm});
            skArc(sketch, "E211.MirrorCS", {"start": v(-91.6, -86.5) * mm, "mid": v(-86.98, -80.3) * mm, "end": v(-82.82, -86.83) * mm});
            skArc(sketch, "E212.MirrorCS", {"start": v(92.18, -102.17) * mm, "mid": v(88.02, -108.7) * mm, "end": v(83.4, -102.5) * mm});
            skPoint(sketch, "E213.MirrorP", {"position": v(8.68, -23.61) * mm});
            skArc(sketch, "E214.MirrorCS", {"start": v(-79.83, -99.18) * mm, "mid": v(-73.3, -95.02) * mm, "end": v(-79.5, -90.4) * mm});
            skLineSegment(sketch, "E215.MirrorCS", {"start": v(-12.35, -24.7) * mm, "end": v(-87.5, -94.5) * mm, "construction": true});
            skPoint(sketch, "E216.MirrorP", {"position": v(-8.68, -23.61) * mm});
            skArc(sketch, "E217.MirrorCS", {"start": v(-92.18, -102.17) * mm, "mid": v(-88.02, -108.7) * mm, "end": v(-83.4, -102.5) * mm});
            skArc(sketch, "E218.MirrorCS", {"start": v(91.6, -86.5) * mm, "mid": v(86.98, -80.3) * mm, "end": v(82.82, -86.83) * mm});
            skPoint(sketch, "E219.MirrorP", {"position": v(-11, -21.12) * mm});
            skPoint(sketch, "E220.MirrorP", {"position": v(11, -21.12) * mm});
            skLineSegment(sketch, "E221.MirrorCS", {"start": v(12.35, -24.7) * mm, "end": v(87.5, -94.5) * mm, "construction": true});
            skArc(sketch, "E222.MirrorCS", {"start": v(95.5, -98.6) * mm, "mid": v(101.7, -93.98) * mm, "end": v(95.17, -89.82) * mm});
            skLineSegment(sketch, "E223.MirrorCS", {"start": v(14.64, -20) * mm, "end": v(82.78, -83.29) * mm});
            skLineSegment(sketch, "E224.MirrorCS", {"start": v(-75.97, -90.61) * mm, "end": v(-7.83, -27.33) * mm});
            skLineSegment(sketch, "E225.MirrorCS", {"start": v(75.97, -90.61) * mm, "end": v(7.83, -27.33) * mm});
            skArc(sketch, "E226.MirrorCS", {"start": v(79.83, -99.18) * mm, "mid": v(73.3, -95.02) * mm, "end": v(79.5, -90.4) * mm});
            skArc(sketch, "E227.MirrorCS", {"start": v(-95.5, -98.6) * mm, "mid": v(-101.7, -93.98) * mm, "end": v(-95.17, -89.82) * mm});
            skLineSegment(sketch, "E228.MirrorCS", {"start": v(-14.64, -20) * mm, "end": v(-82.78, -83.29) * mm});
            skSolve(sketch);
        }
        {
            var Q0;
            Q0 = qSketchRegion(id + "F13", true);
            extrude(context, id + "F14", {"entities" : qUnion([Q0]), "depth" : 4 * mm, "offsetDistance" : 25 * mm});
        }
        {
            var Q0;
            Q0=qCreatedBy(id+"F12.planeOp",FACE);
            cPlane(context, id + "F15", {"entities" : qUnion([Q0]), "cplaneType" : CPlaneType.OFFSET, "offset" : 0 * mm, "width" : 150 * mm, "height" : 150 * mm});
        }
        {
            var Q0;
            Q0=qCreatedBy(id+"F15.planeOp",FACE);
            var sketch = newSketch(context, id + "F16", { "sketchPlane" : qUnion([Q0])});
            skLineSegment(sketch, "E229.bottom", {"start": v(-13, 18) * mm, "end": v(13, 18) * mm});
            skLineSegment(sketch, "E229.top", {"start": v(-13, -18) * mm, "end": v(13, -18) * mm});
            skLineSegment(sketch, "E229.left", {"start": v(-18, 13) * mm, "end": v(-18, -13) * mm});
            skLineSegment(sketch, "E229.right", {"start": v(18, 13) * mm, "end": v(18, -13) * mm});
            skPoint(sketch, "E230.visualSharp", {"position": v(-18, 18) * mm});
            skArc(sketch, "E230.filletArc", {"start": v(-13, 18) * mm, "mid": v(-16.54, 16.54) * mm, "end": v(-18, 13) * mm});
            skPoint(sketch, "E231.visualSharp", {"position": v(18, 18) * mm});
            skArc(sketch, "E231.filletArc", {"start": v(18, 13) * mm, "mid": v(16.54, 16.54) * mm, "end": v(13, 18) * mm});
            skPoint(sketch, "E232.visualSharp", {"position": v(18, -18) * mm});
            skArc(sketch, "E232.filletArc", {"start": v(13, -18) * mm, "mid": v(16.54, -16.54) * mm, "end": v(18, -13) * mm});
            skPoint(sketch, "E233.visualSharp", {"position": v(-18, -18) * mm});
            skArc(sketch, "E233.filletArc", {"start": v(-18, -13) * mm, "mid": v(-16.54, -16.54) * mm, "end": v(-13, -18) * mm});
            skCircle(sketch, "E234", {"center": v(-13, 13) * mm, "radius": 1.7 * mm});
            skCircle(sketch, "E235", {"center": v(13, 13) * mm, "radius": 1.7 * mm});
            skCircle(sketch, "E236", {"center": v(13, -13) * mm, "radius": 1.7 * mm});
            skCircle(sketch, "E237", {"center": v(-13, -13) * mm, "radius": 1.7 * mm});
            skSolve(sketch);
        }
        {
            var Q0;
            Q0 = qSketchRegion(id + "F16", true);
            extrude(context, id + "F17", {"entities" : qUnion([Q0]), "depth" : 10 * mm, "offsetDistance" : 25 * mm});
        }
        {
            var Q0;
            Q0=qCreatedBy(id+"F12.planeOp",FACE);
            var sketch = newSketch(context, id + "F18", { "sketchPlane" : qUnion([Q0])});
            skCircle(sketch, "E238", {"center": v(-13, 13) * mm, "radius": 1.7 * mm});
            skCircle(sketch, "E239", {"center": v(13, 13) * mm, "radius": 1.7 * mm});
            skCircle(sketch, "E240", {"center": v(13, -13) * mm, "radius": 1.7 * mm});
            skCircle(sketch, "E241", {"center": v(-13, -13) * mm, "radius": 1.7 * mm});
            skCircle(sketch, "E242", {"center": v(-25.54, 36.95) * mm, "radius": 1.7 * mm});
            skArc(sketch, "E243", {"start": v(-28.94, 33.29) * mm, "mid": v(-29.2, 40.36) * mm, "end": v(-22.14, 40.62) * mm});
            skArc(sketch, "E244", {"start": v(-18, 13) * mm, "mid": v(-17.9, 12.05) * mm, "end": v(-17.64, 11.14) * mm});
            skArc(sketch, "E245", {"start": v(-18, -13) * mm, "mid": v(-17.9, -12.05) * mm, "end": v(-17.64, -11.14) * mm});
            skArc(sketch, "E246", {"start": v(-17.64, -11.14) * mm, "mid": v(-15.5, 0) * mm, "end": v(-17.64, 11.14) * mm});
            skArc(sketch, "E247", {"start": v(-28.94, -33.29) * mm, "mid": v(-29.2, -40.36) * mm, "end": v(-22.14, -40.62) * mm});
            skArc(sketch, "E248", {"start": v(28.94, 33.29) * mm, "mid": v(29.2, 40.36) * mm, "end": v(22.14, 40.62) * mm});
            skArc(sketch, "E249", {"start": v(17.64, 11.14) * mm, "mid": v(15.5, 0) * mm, "end": v(17.64, -11.14) * mm});
            skArc(sketch, "E250", {"start": v(18, 13) * mm, "mid": v(17.9, 12.05) * mm, "end": v(17.64, 11.14) * mm});
            skArc(sketch, "E251", {"start": v(17.64, -11.14) * mm, "mid": v(17.9, -12.05) * mm, "end": v(18, -13) * mm});
            skArc(sketch, "E252", {"start": v(22.14, -40.62) * mm, "mid": v(29.2, -40.36) * mm, "end": v(28.94, -33.29) * mm});
            skCircle(sketch, "E253", {"center": v(25.54, 36.95) * mm, "radius": 1.7 * mm});
            skCircle(sketch, "E254", {"center": v(25.54, -36.95) * mm, "radius": 1.7 * mm});
            skCircle(sketch, "E255", {"center": v(-25.54, -36.95) * mm, "radius": 1.7 * mm});
            skCircle(sketch, "E256", {"center": v(0, 20.18) * mm, "radius": 5 * mm});
            skCircle(sketch, "E257", {"center": v(0, -20.18) * mm, "radius": 5 * mm});
            skCircle(sketch, "E258", {"center": v(0, 0) * mm, "radius": 5 * mm});
            skLineSegment(sketch, "E259", {"start": v(-28.94, 33.29) * mm, "end": v(-24.55, 29.2) * mm});
            skArc(sketch, "E260", {"start": v(-18, 13) * mm, "mid": v(-19.47, 21.83) * mm, "end": v(-24.55, 29.2) * mm});
            skLineSegment(sketch, "E261", {"start": v(-22.14, 40.62) * mm, "end": v(-19, 37.7) * mm});
            skLineSegment(sketch, "E262", {"start": v(-19, 37.7) * mm, "end": v(-19, 47.7) * mm});
            skLineSegment(sketch, "E263", {"start": v(19, 56.7) * mm, "end": v(19, 53.7) * mm});
            skLineSegment(sketch, "E264", {"start": v(22.14, 40.62) * mm, "end": v(19, 37.7) * mm});
            skLineSegment(sketch, "E265", {"start": v(28.94, 33.29) * mm, "end": v(24.55, 29.2) * mm});
            skArc(sketch, "E266", {"start": v(24.55, 29.2) * mm, "mid": v(19.47, 21.83) * mm, "end": v(18, 13) * mm});
            skLineSegment(sketch, "E267", {"start": v(-28.94, -33.29) * mm, "end": v(-24.55, -29.2) * mm});
            skArc(sketch, "E268", {"start": v(-24.55, -29.2) * mm, "mid": v(-19.47, -21.83) * mm, "end": v(-18, -13) * mm});
            skLineSegment(sketch, "E269", {"start": v(28.94, -33.29) * mm, "end": v(24.55, -29.2) * mm});
            skArc(sketch, "E270", {"start": v(18, -13) * mm, "mid": v(19.47, -21.83) * mm, "end": v(24.55, -29.2) * mm});
            skLineSegment(sketch, "E271", {"start": v(-22.14, -40.62) * mm, "end": v(-17.74, -36.53) * mm});
            skLineSegment(sketch, "E272", {"start": v(22.14, -40.62) * mm, "end": v(17.74, -36.53) * mm});
            skArc(sketch, "E273", {"start": v(17.74, -36.53) * mm, "mid": v(0, -29.56) * mm, "end": v(-17.74, -36.53) * mm});
            skLineSegment(sketch, "E274.bottom", {"start": v(-19, 52.7) * mm, "end": v(-21, 52.7) * mm});
            skLineSegment(sketch, "E274.top", {"start": v(-19, 48.7) * mm, "end": v(-21, 48.7) * mm});
            skLineSegment(sketch, "E274.right", {"start": v(-21, 52.7) * mm, "end": v(-21, 48.7) * mm});
            skArc(sketch, "E275", {"start": v(-19, 52.7) * mm, "mid": v(-18.5, 53.2) * mm, "end": v(-19, 53.7) * mm});
            skArc(sketch, "E276", {"start": v(-19, 48.7) * mm, "mid": v(-18.5, 48.2) * mm, "end": v(-19, 47.7) * mm});
            skLineSegment(sketch, "E277.trimOffspring", {"start": v(-19, 53.7) * mm, "end": v(-19, 56.7) * mm});
            skLineSegment(sketch, "E278.bottom", {"start": v(19, 52.7) * mm, "end": v(21, 52.7) * mm});
            skLineSegment(sketch, "E278.top", {"start": v(19, 48.7) * mm, "end": v(21, 48.7) * mm});
            skLineSegment(sketch, "E278.right", {"start": v(21, 52.7) * mm, "end": v(21, 48.7) * mm});
            skLineSegment(sketch, "E279.trimOffspring", {"start": v(19, 47.7) * mm, "end": v(19, 37.7) * mm});
            skArc(sketch, "E280", {"start": v(-19, 56.7) * mm, "mid": v(-17.44, 58.65) * mm, "end": v(-15.19, 57.55) * mm});
            skArc(sketch, "E281", {"start": v(19, 56.7) * mm, "mid": v(17.44, 58.65) * mm, "end": v(15.19, 57.55) * mm});
            skLineSegment(sketch, "E282", {"start": v(-15.19, 57.55) * mm, "end": v(-4.53, 34.82) * mm});
            skPoint(sketch, "E283.visualSharp", {"position": v(0, 25.18) * mm});
            skArc(sketch, "E283.filletArc", {"start": v(-4.53, 34.82) * mm, "mid": v(0, 31.95) * mm, "end": v(4.53, 34.82) * mm});
            skArc(sketch, "E284", {"start": v(19, 52.7) * mm, "mid": v(18.5, 53.2) * mm, "end": v(19, 53.7) * mm});
            skArc(sketch, "E285", {"start": v(19, 48.7) * mm, "mid": v(18.5, 48.2) * mm, "end": v(19, 47.7) * mm});
            skLineSegment(sketch, "E286", {"start": v(15.19, 57.55) * mm, "end": v(4.53, 34.82) * mm});
            skSolve(sketch);
        }
        {
            var Q0;
            Q0 = qSketchRegion(id + "F18", true);
            extrude(context, id + "F19", {"entities" : qUnion([Q0]), "oppositeDirection" : true, "depth" : 3 * mm, "offsetDistance" : 25 * mm});
        }
        {
            var Q0;
            Q0=qCreatedBy(id+"F9.planeOp",FACE);
            var sketch = newSketch(context, id + "F20", { "sketchPlane" : qUnion([Q0])});
            skLineSegment(sketch, "E287.bottom", {"start": v(40.15, 30.7) * mm, "end": v(37.85, 30.7) * mm});
            skLineSegment(sketch, "E287.top", {"start": v(40.15, 26.4) * mm, "end": v(37.85, 26.4) * mm});
            skLineSegment(sketch, "E287.left", {"start": v(40.15, 30.7) * mm, "end": v(40.15, 26.4) * mm});
            skLineSegment(sketch, "E287.right", {"start": v(37.85, 30.7) * mm, "end": v(37.85, 26.4) * mm});
            skLineSegment(sketch, "E288.bottom", {"start": v(40.15, 11.6) * mm, "end": v(37.85, 11.6) * mm});
            skLineSegment(sketch, "E288.top", {"start": v(40.15, 7.3) * mm, "end": v(37.85, 7.3) * mm});
            skLineSegment(sketch, "E288.left", {"start": v(40.15, 11.6) * mm, "end": v(40.15, 7.3) * mm});
            skLineSegment(sketch, "E288.right", {"start": v(37.85, 11.6) * mm, "end": v(37.85, 7.3) * mm});
            skArc(sketch, "E289", {"start": v(40.15, 30.7) * mm, "mid": v(40.65, 30.2) * mm, "end": v(40.15, 29.7) * mm});
            skArc(sketch, "E290", {"start": v(37.85, 30.7) * mm, "mid": v(37.35, 30.2) * mm, "end": v(37.85, 29.7) * mm});
            skArc(sketch, "E291", {"start": v(37.85, 26.4) * mm, "mid": v(37.35, 26.9) * mm, "end": v(37.85, 27.4) * mm});
            skArc(sketch, "E292", {"start": v(40.15, 26.4) * mm, "mid": v(40.65, 26.9) * mm, "end": v(40.15, 27.4) * mm});
            skArc(sketch, "E293", {"start": v(40.15, 11.6) * mm, "mid": v(40.65, 11.1) * mm, "end": v(40.15, 10.6) * mm});
            skArc(sketch, "E294", {"start": v(37.85, 11.6) * mm, "mid": v(37.35, 11.1) * mm, "end": v(37.85, 10.6) * mm});
            skArc(sketch, "E295", {"start": v(37.85, 7.3) * mm, "mid": v(37.35, 7.8) * mm, "end": v(37.85, 8.3) * mm});
            skArc(sketch, "E296", {"start": v(40.15, 7.3) * mm, "mid": v(40.65, 7.8) * mm, "end": v(40.15, 8.3) * mm});
            skLineSegment(sketch, "E297", {"start": v(38, 38) * mm, "end": v(62.33, 49.34) * mm});
            skCircle(sketch, "E298", {"center": v(64.31, 45.08) * mm, "radius": 1.7 * mm});
            skLineSegment(sketch, "E299", {"start": v(59.02, 17.77) * mm, "end": v(84.4, 27) * mm, "construction": true});
            skLineSegment(sketch, "E300", {"start": v(86.79, 20.43) * mm, "end": v(82, 33.59) * mm, "construction": true});
            skLineSegment(sketch, "E301", {"start": v(63.9, 4.38) * mm, "end": v(54.15, 31.16) * mm, "construction": true});
            skPoint(sketch, "E302", {"position": v(61.84, 18.8) * mm});
            skCircle(sketch, "E303", {"center": v(64.31, 45.08) * mm, "radius": 3 * mm, "construction": true});
            skLineSegment(sketch, "E304", {"start": v(64.31, 45.08) * mm, "end": v(62.33, 49.34) * mm, "construction": true});
            skArc(sketch, "E305", {"start": v(62.33, 49.34) * mm, "mid": v(64.22, 49.78) * mm, "end": v(66.14, 49.42) * mm});
            skCircle(sketch, "E306", {"center": v(61.84, 18.8) * mm, "radius": 25 * mm, "construction": true});
            skArc(sketch, "E307", {"start": v(86.79, 20.43) * mm, "mid": v(80.58, 37.86) * mm, "end": v(66.14, 49.42) * mm});
            skCircle(sketch, "E308", {"center": v(51.05, 4.87) * mm, "radius": 1.7 * mm});
            skCircle(sketch, "E309", {"center": v(51.05, 4.87) * mm, "radius": 3 * mm, "construction": true});
            skLineSegment(sketch, "E310", {"start": v(40, -13.15) * mm, "end": v(48.15, -13.15) * mm});
            skArc(sketch, "E311", {"start": v(48.15, -13.15) * mm, "mid": v(73.75, -3.58) * mm, "end": v(86.79, 20.43) * mm});
            skCircle(sketch, "E312", {"center": v(64.31, 45.08) * mm, "radius": 4.7 * mm});
            skLineSegment(sketch, "E313", {"start": v(59.62, 44.77) * mm, "end": v(44.15, 37.56) * mm});
            skLineSegment(sketch, "E314", {"start": v(44.15, 37.56) * mm, "end": v(44.15, 7.98) * mm});
            skArc(sketch, "E315", {"start": v(69, 44.6) * mm, "mid": v(79.25, 34.44) * mm, "end": v(83.76, 20.72) * mm});
            skArc(sketch, "E316", {"start": v(83.76, 20.72) * mm, "mid": v(76.67, 3.94) * mm, "end": v(62.28, -7.22) * mm});
            skCircle(sketch, "E317", {"center": v(51.05, 4.87) * mm, "radius": 4.7 * mm});
            skArc(sketch, "E318", {"start": v(62.28, -7.22) * mm, "mid": v(60.03, -0.97) * mm, "end": v(55.67, 4.04) * mm});
            skPoint(sketch, "E319.orphan", {"position": v(44.15, 4.58) * mm});
            skArc(sketch, "E320.trimOffspring", {"start": v(47.33, 7.74) * mm, "mid": v(45.74, 7.93) * mm, "end": v(44.15, 7.98) * mm});
            skLineSegment(sketch, "E321", {"start": v(40, -10.15) * mm, "end": v(40, -2.85) * mm});
            skLineSegment(sketch, "E322.left", {"start": v(52.85, -6.85) * mm, "end": v(52.85, -10.15) * mm});
            skLineSegment(sketch, "E322.right", {"start": v(48.55, -6.85) * mm, "end": v(48.55, -10.15) * mm});
            skLineSegment(sketch, "E323", {"start": v(48.55, -8.5) * mm, "end": v(52.85, -8.5) * mm, "construction": true});
            skArc(sketch, "E324", {"start": v(48.55, -6.85) * mm, "mid": v(49.05, -6.35) * mm, "end": v(49.55, -6.85) * mm});
            skArc(sketch, "E325", {"start": v(52.85, -6.85) * mm, "mid": v(52.35, -6.35) * mm, "end": v(51.85, -6.85) * mm});
            skArc(sketch, "E326", {"start": v(52.85, -10.15) * mm, "mid": v(52.35, -10.65) * mm, "end": v(51.85, -10.15) * mm});
            skArc(sketch, "E327", {"start": v(48.55, -10.15) * mm, "mid": v(49.05, -10.65) * mm, "end": v(49.55, -10.15) * mm});
            skLineSegment(sketch, "E328.trimOffspring", {"start": v(51.85, -10.15) * mm, "end": v(49.55, -10.15) * mm});
            skLineSegment(sketch, "E329", {"start": v(51.85, -6.85) * mm, "end": v(49.55, -6.85) * mm});
            skLineSegment(sketch, "E330.bottom", {"start": v(40, -13.15) * mm, "end": v(26, -13.15) * mm});
            skLineSegment(sketch, "E330.top", {"start": v(40, -10.15) * mm, "end": v(26, -10.15) * mm});
            skLineSegment(sketch, "E330.right", {"start": v(26, -13.15) * mm, "end": v(26, -10.15) * mm});
            skLineSegment(sketch, "E331.left", {"start": v(34.15, 5.15) * mm, "end": v(34.15, 2.85) * mm});
            skLineSegment(sketch, "E331.right", {"start": v(29.85, 5.15) * mm, "end": v(29.85, 2.85) * mm});
            skArc(sketch, "E332", {"start": v(29.85, 2.85) * mm, "mid": v(30.35, 2.35) * mm, "end": v(30.85, 2.85) * mm});
            skArc(sketch, "E333", {"start": v(34.15, 2.85) * mm, "mid": v(33.65, 2.35) * mm, "end": v(33.15, 2.85) * mm});
            skArc(sketch, "E334", {"start": v(34.15, 5.15) * mm, "mid": v(33.65, 5.65) * mm, "end": v(33.15, 5.15) * mm});
            skArc(sketch, "E335", {"start": v(29.85, 5.15) * mm, "mid": v(30.35, 5.65) * mm, "end": v(30.85, 5.15) * mm});
            skLineSegment(sketch, "E336.trimOffspring", {"start": v(33.15, 2.85) * mm, "end": v(30.85, 2.85) * mm});
            skLineSegment(sketch, "E337", {"start": v(33.15, 5.15) * mm, "end": v(30.85, 5.15) * mm});
            skArc(sketch, "E338", {"start": v(38, 38) * mm, "mid": v(29.08, 18.43) * mm, "end": v(26, -2.85) * mm});
            skLineSegment(sketch, "E339", {"start": v(40, -2.85) * mm, "end": v(26, -2.85) * mm});
            skSolve(sketch);
        }
        {
            var Q0;
            Q0=makeQuery(id+"F20.imprint","IMPRINT",FACE,{"disambiguationData":[TD([[makeQuery(id+"F20.imprint","IMPRINT",EDGE,{"derivedFrom":sQuery(id+"F20.wireOp",EDGE,"E287.bottom")}),-1.0]])]});
            var Q1;
            {var subQ0=sQuery(id+"F20.wireOp",EDGE,"E318");var subQ1=sQuery(id+"F20.wireOp",EDGE,"E308");var subQ2=makeQuery(id+"F20.imprint","INTERSECT",VERTEX,{"derivedFrom":[subQ1,subQ0]});Q1=makeQuery(id+"F20.imprint","IMPRINT",FACE,{"disambiguationData":[TD([[makeQuery(id+"F20.imprint","IMPRINT",EDGE,{"disambiguationData":[TD([[subQ2,1.0]])],"derivedFrom":subQ1}),-1.0]])]});}
            var Q2;
            {var subQ0=sQuery(id+"F20.wireOp",EDGE,"E318");var subQ1=sQuery(id+"F20.wireOp",EDGE,"E317");var subQ2=makeQuery(id+"F20.imprint","INTERSECT",VERTEX,{"disambiguationData":[OD(0.0)],"derivedFrom":[subQ1,subQ0]});Q2=makeQuery(id+"F20.imprint","IMPRINT",FACE,{"disambiguationData":[TD([[makeQuery(id+"F20.imprint","IMPRINT",EDGE,{"disambiguationData":[TD([[subQ2,1.0]])],"derivedFrom":subQ1}),1.0]])]});}
            var Q3;
            {var subQ0=sQuery(id+"F20.wireOp",EDGE,"E318");var subQ1=sQuery(id+"F20.wireOp",EDGE,"E308");var subQ2=makeQuery(id+"F20.imprint","INTERSECT",VERTEX,{"derivedFrom":[subQ1,subQ0]});Q3=makeQuery(id+"F20.imprint","IMPRINT",FACE,{"disambiguationData":[TD([[makeQuery(id+"F20.imprint","IMPRINT",EDGE,{"disambiguationData":[TD([[subQ2,-1.0]])],"derivedFrom":subQ1}),-1.0]])]});}
            var Q4;
            {var subQ0=sQuery(id+"F20.wireOp",EDGE,"fjiXCNpH-yBTj-5JCt-CiLw-xY1FPNxqiV29");var subQ1=sQuery(id+"F20.wireOp",EDGE,"E317");var subQ2=makeQuery(id+"F20.imprint","INTERSECT",VERTEX,{"disambiguationData":[OD(0.0)],"derivedFrom":[subQ1,subQ0]});Q4=makeQuery(id+"F20.imprint","IMPRINT",FACE,{"disambiguationData":[TD([[makeQuery(id+"F20.imprint","IMPRINT",EDGE,{"disambiguationData":[TD([[subQ2,-1.0]])],"derivedFrom":subQ1}),1.0]])]});}
            var Q5;
            Q5=makeQuery(id+"F20.imprint","IMPRINT",FACE,{"disambiguationData":[TD([[makeQuery(id+"F20.imprint","IMPRINT",EDGE,{"derivedFrom":sQuery(id+"F20.wireOp",EDGE,"E298")}),-1.0]])]});
            extrude(context, id + "F21", {"entities" : qUnion([Q0, Q1, Q2, Q3, Q4, Q5]), "oppositeDirection" : true, "depth" : 2 * mm, "offsetDistance" : 25 * mm});
        }
        {
            var Q0;
            Q0=makeQuery(id+"F21.opExtrude","SWEPT_BODY",BODY,{"disambiguationData":[OSD([sQuery(id+"F20.wireOp",EDGE,"E287.bottom"),sQuery(id+"F20.wireOp",EDGE,"E287.top"),sQuery(id+"F20.wireOp",EDGE,"E287.left"),sQuery(id+"F20.wireOp",EDGE,"E287.right"),sQuery(id+"F20.wireOp",EDGE,"E288.bottom"),sQuery(id+"F20.wireOp",EDGE,"E288.top"),sQuery(id+"F20.wireOp",EDGE,"E288.left"),sQuery(id+"F20.wireOp",EDGE,"E288.right"),sQuery(id+"F20.wireOp",EDGE,"E289"),sQuery(id+"F20.wireOp",EDGE,"E290"),sQuery(id+"F20.wireOp",EDGE,"E291"),sQuery(id+"F20.wireOp",EDGE,"E292"),sQuery(id+"F20.wireOp",EDGE,"E293"),sQuery(id+"F20.wireOp",EDGE,"E294"),sQuery(id+"F20.wireOp",EDGE,"E295"),sQuery(id+"F20.wireOp",EDGE,"E296"),sQuery(id+"F20.wireOp",EDGE,"yR4Bzr1t-1Bwp-EEH0-Oxtx-5w5kcoDZ2t11"),sQuery(id+"F20.wireOp",EDGE,"E297"),sQuery(id+"F20.wireOp",EDGE,"E298"),sQuery(id+"F20.wireOp",EDGE,"E307"),sQuery(id+"F20.wireOp",EDGE,"E308"),sQuery(id+"F20.wireOp",EDGE,"E310"),sQuery(id+"F20.wireOp",EDGE,"E311"),sQuery(id+"F20.wireOp",EDGE,"E312"),sQuery(id+"F20.wireOp",EDGE,"E313"),sQuery(id+"F20.wireOp",EDGE,"E314"),sQuery(id+"F20.wireOp",EDGE,"E315"),sQuery(id+"F20.wireOp",EDGE,"E316"),sQuery(id+"F20.wireOp",EDGE,"E317"),sQuery(id+"F20.wireOp",EDGE,"E318"),sQuery(id+"F20.wireOp",EDGE,"E320.trimOffspring"),sQuery(id+"F20.wireOp",EDGE,"PmIOwoAA-JQof-I90y-mSRn-52ZyVsivZStj"),sQuery(id+"F20.wireOp",EDGE,"E321"),sQuery(id+"F20.wireOp",EDGE,"E322.left"),sQuery(id+"F20.wireOp",EDGE,"E322.right"),sQuery(id+"F20.wireOp",EDGE,"E324"),sQuery(id+"F20.wireOp",EDGE,"E325"),sQuery(id+"F20.wireOp",EDGE,"E326"),sQuery(id+"F20.wireOp",EDGE,"E327"),sQuery(id+"F20.wireOp",EDGE,"E328.trimOffspring"),sQuery(id+"F20.wireOp",EDGE,"E329"),sQuery(id+"F20.wireOp",EDGE,"E330.bottom"),sQuery(id+"F20.wireOp",EDGE,"E330.top"),sQuery(id+"F20.wireOp",EDGE,"E330.right")])]});
            var Q1;
            Q1=qCreatedBy(makeId("Right.planeOp"),FACE);
            mirror(context, id + "F22", {"entities" : qUnion([Q0]), "mirrorPlane" : qUnion([Q1])});
        }
        {
            var Q0;
            Q0=makeQuery(id+"F17.opExtrude","CAP_FACE",FACE,{"disambiguationData":[OSD([sQuery(id+"F16.wireOp",EDGE,"E229.bottom"),sQuery(id+"F16.wireOp",EDGE,"E229.top"),sQuery(id+"F16.wireOp",EDGE,"E229.left"),sQuery(id+"F16.wireOp",EDGE,"E229.right"),sQuery(id+"F16.wireOp",EDGE,"E230.filletArc"),sQuery(id+"F16.wireOp",EDGE,"E231.filletArc"),sQuery(id+"F16.wireOp",EDGE,"E232.filletArc"),sQuery(id+"F16.wireOp",EDGE,"E233.filletArc"),sQuery(id+"F16.wireOp",EDGE,"E234"),sQuery(id+"F16.wireOp",EDGE,"E235"),sQuery(id+"F16.wireOp",EDGE,"E236"),sQuery(id+"F16.wireOp",EDGE,"E237")])],"isStart":false});
            cPlane(context, id + "F23", {"entities" : qUnion([Q0]), "cplaneType" : CPlaneType.OFFSET, "offset" : 0 * mm, "width" : 150 * mm, "height" : 150 * mm});
        }
        {
            var Q0;
            Q0=qCreatedBy(id+"F23.planeOp",FACE);
            var sketch = newSketch(context, id + "F24", { "sketchPlane" : qUnion([Q0])});
            skCircle(sketch, "E340", {"center": v(-12.35, 24.7) * mm, "radius": 1.7 * mm});
            skCircle(sketch, "E341", {"center": v(12.35, 24.7) * mm, "radius": 1.7 * mm});
            skCircle(sketch, "E342", {"center": v(12.35, -24.7) * mm, "radius": 1.7 * mm});
            skCircle(sketch, "E343", {"center": v(-12.35, -24.7) * mm, "radius": 1.7 * mm});
            skLineSegment(sketch, "E344.top", {"start": v(-12.35, -31.35) * mm, "end": v(12.35, -31.35) * mm});
            skLineSegment(sketch, "E344.right", {"start": v(19, 29) * mm, "end": v(19, -24.7) * mm});
            skPoint(sketch, "E345.visualSharp", {"position": v(-19, -31.35) * mm});
            skArc(sketch, "E345.filletArc", {"start": v(-19, -24.7) * mm, "mid": v(-17.05, -29.4) * mm, "end": v(-12.35, -31.35) * mm});
            skPoint(sketch, "E346.visualSharp", {"position": v(19, -31.35) * mm});
            skArc(sketch, "E346.filletArc", {"start": v(12.35, -31.35) * mm, "mid": v(17.05, -29.4) * mm, "end": v(19, -24.7) * mm});
            skLineSegment(sketch, "E347.bottom", {"start": v(21, 34) * mm, "end": v(-21, 34) * mm});
            skLineSegment(sketch, "E347.top", {"start": v(-19, 30) * mm, "end": v(-21, 30) * mm});
            skLineSegment(sketch, "E347.right", {"start": v(-21, 34) * mm, "end": v(-21, 30) * mm});
            skArc(sketch, "E348", {"start": v(-19, 30) * mm, "mid": v(-18.5, 29.5) * mm, "end": v(-19, 29) * mm});
            skLineSegment(sketch, "E349.trimOffspring", {"start": v(-19, 29) * mm, "end": v(-19, -24.7) * mm});
            skLineSegment(sketch, "E350", {"start": v(19, 30) * mm, "end": v(21, 30) * mm});
            skLineSegment(sketch, "E351", {"start": v(21, 30) * mm, "end": v(21, 34) * mm});
            skArc(sketch, "E352", {"start": v(19, 30) * mm, "mid": v(18.5, 29.5) * mm, "end": v(19, 29) * mm});
            skArc(sketch, "E353", {"start": v(-10.25, 30) * mm, "mid": v(-7.17, 22.32) * mm, "end": v(-15, 19.65) * mm});
            skArc(sketch, "E354", {"start": v(10.25, 30) * mm, "mid": v(7.17, 22.32) * mm, "end": v(15, 19.65) * mm});
            skArc(sketch, "E355", {"start": v(-15, -19.65) * mm, "mid": v(-8.32, -20.67) * mm, "end": v(-7.3, -27.35) * mm});
            skArc(sketch, "E356", {"start": v(15, -19.65) * mm, "mid": v(8.32, -20.67) * mm, "end": v(7.3, -27.35) * mm});
            skLineSegment(sketch, "E357", {"start": v(-15, 19.65) * mm, "end": v(-15, 13.83) * mm});
            skLineSegment(sketch, "E358", {"start": v(15, 19.65) * mm, "end": v(15, 13.83) * mm});
            skLineSegment(sketch, "E359", {"start": v(-7.3, -27.35) * mm, "end": v(7.3, -27.35) * mm});
            skLineSegment(sketch, "E360", {"start": v(-10.25, 30) * mm, "end": v(10.25, 30) * mm});
            skLineSegment(sketch, "E361", {"start": v(-15, 13.83) * mm, "end": v(0, 1.92) * mm});
            skLineSegment(sketch, "E362", {"start": v(-15, 10) * mm, "end": v(-2.41, 0) * mm});
            skLineSegment(sketch, "E363", {"start": v(15, 13.83) * mm, "end": v(0, 1.92) * mm});
            skLineSegment(sketch, "E364", {"start": v(15, 10) * mm, "end": v(2.41, 0) * mm});
            skLineSegment(sketch, "E365.trimOffspring", {"start": v(15, -13.83) * mm, "end": v(15, -19.65) * mm});
            skLineSegment(sketch, "E366.trimOffspring", {"start": v(15, 10) * mm, "end": v(15, -10) * mm});
            skLineSegment(sketch, "E367.trimOffspring", {"start": v(-15, 10) * mm, "end": v(-15, -10) * mm});
            skLineSegment(sketch, "E368.trimOffspring", {"start": v(-15, -13.83) * mm, "end": v(-15, -19.65) * mm});
            skLineSegment(sketch, "E369.trimOffspring", {"start": v(0, -1.92) * mm, "end": v(15, -13.83) * mm});
            skLineSegment(sketch, "E370.trimOffspring", {"start": v(2.41, 0) * mm, "end": v(15, -10) * mm});
            skLineSegment(sketch, "E371.trimOffspring", {"start": v(0, -1.92) * mm, "end": v(-15, -13.83) * mm});
            skLineSegment(sketch, "E372.trimOffspring", {"start": v(-2.41, 0) * mm, "end": v(-15, -10) * mm});
            skSolve(sketch);
        }
        {
            var Q0;
            Q0 = qSketchRegion(id + "F24", true);
            extrude(context, id + "F25", {"entities" : qUnion([Q0]), "depth" : 2 * mm, "offsetDistance" : 25 * mm});
        }
        {
            var Q0;
            Q0=qCreatedBy(id+"F10.planeOp",FACE);
            var sketch = newSketch(context, id + "F26", { "sketchPlane" : qUnion([Q0])});
            skCircle(sketch, "E373", {"center": v(-12.35, 24.7) * mm, "radius": 1.7 * mm});
            skCircle(sketch, "E374", {"center": v(-12.35, 24.7) * mm, "radius": 3 * mm});
            skCircle(sketch, "E375", {"center": v(12.35, 24.7) * mm, "radius": 1.7 * mm});
            skCircle(sketch, "E376", {"center": v(12.35, 24.7) * mm, "radius": 3 * mm});
            skCircle(sketch, "E377", {"center": v(12.35, -24.7) * mm, "radius": 1.7 * mm});
            skCircle(sketch, "E378", {"center": v(12.35, -24.7) * mm, "radius": 3 * mm});
            skCircle(sketch, "E379", {"center": v(-12.35, -24.7) * mm, "radius": 1.7 * mm});
            skCircle(sketch, "E380", {"center": v(-12.35, -24.7) * mm, "radius": 3 * mm});
            skSolve(sketch);
        }
        {
            var Q0;
            Q0 = qSketchRegion(id + "F26", true);
            extrude(context, id + "F27", {"entities" : qUnion([Q0]), "depth" : 6 * mm, "offsetDistance" : 25 * mm});
        }
        {
            var Q0;
            Q0=makeQuery(id+"F21.opExtrude","CAP_FACE",FACE,{"disambiguationData":[OSD([sQuery(id+"F20.wireOp",EDGE,"E287.bottom"),sQuery(id+"F20.wireOp",EDGE,"E287.top"),sQuery(id+"F20.wireOp",EDGE,"E287.left"),sQuery(id+"F20.wireOp",EDGE,"E287.right"),sQuery(id+"F20.wireOp",EDGE,"E288.bottom"),sQuery(id+"F20.wireOp",EDGE,"E288.top"),sQuery(id+"F20.wireOp",EDGE,"E288.left"),sQuery(id+"F20.wireOp",EDGE,"E288.right"),sQuery(id+"F20.wireOp",EDGE,"E289"),sQuery(id+"F20.wireOp",EDGE,"E290"),sQuery(id+"F20.wireOp",EDGE,"E291"),sQuery(id+"F20.wireOp",EDGE,"E292"),sQuery(id+"F20.wireOp",EDGE,"E293"),sQuery(id+"F20.wireOp",EDGE,"E294"),sQuery(id+"F20.wireOp",EDGE,"E295"),sQuery(id+"F20.wireOp",EDGE,"E296"),sQuery(id+"F20.wireOp",EDGE,"E297"),sQuery(id+"F20.wireOp",EDGE,"E298"),sQuery(id+"F20.wireOp",EDGE,"E307"),sQuery(id+"F20.wireOp",EDGE,"E308"),sQuery(id+"F20.wireOp",EDGE,"E310"),sQuery(id+"F20.wireOp",EDGE,"E311"),sQuery(id+"F20.wireOp",EDGE,"E312"),sQuery(id+"F20.wireOp",EDGE,"E313"),sQuery(id+"F20.wireOp",EDGE,"E314"),sQuery(id+"F20.wireOp",EDGE,"E315"),sQuery(id+"F20.wireOp",EDGE,"E316"),sQuery(id+"F20.wireOp",EDGE,"E317"),sQuery(id+"F20.wireOp",EDGE,"E318"),sQuery(id+"F20.wireOp",EDGE,"E320.trimOffspring"),sQuery(id+"F20.wireOp",EDGE,"E321"),sQuery(id+"F20.wireOp",EDGE,"E322.left"),sQuery(id+"F20.wireOp",EDGE,"E322.right"),sQuery(id+"F20.wireOp",EDGE,"E324"),sQuery(id+"F20.wireOp",EDGE,"E325"),sQuery(id+"F20.wireOp",EDGE,"E326"),sQuery(id+"F20.wireOp",EDGE,"E327"),sQuery(id+"F20.wireOp",EDGE,"E328.trimOffspring"),sQuery(id+"F20.wireOp",EDGE,"E329"),sQuery(id+"F20.wireOp",EDGE,"E330.bottom"),sQuery(id+"F20.wireOp",EDGE,"E330.top"),sQuery(id+"F20.wireOp",EDGE,"E330.right"),sQuery(id+"F20.wireOp",EDGE,"E331.left"),sQuery(id+"F20.wireOp",EDGE,"E331.right"),sQuery(id+"F20.wireOp",EDGE,"E332"),sQuery(id+"F20.wireOp",EDGE,"E333"),sQuery(id+"F20.wireOp",EDGE,"E334"),sQuery(id+"F20.wireOp",EDGE,"E335"),sQuery(id+"F20.wireOp",EDGE,"E336.trimOffspring"),sQuery(id+"F20.wireOp",EDGE,"E337"),sQuery(id+"F20.wireOp",EDGE,"E338"),sQuery(id+"F20.wireOp",EDGE,"E339")])],"isStart":true});
            var sketch = newSketch(context, id + "F28", { "sketchPlane" : qUnion([Q0])});
            skCircle(sketch, "E381", {"center": v(51.05, 4.87) * mm, "radius": 3 * mm});
            skCircle(sketch, "E382", {"center": v(64.31, 45.08) * mm, "radius": 3 * mm});
            skCircle(sketch, "E383", {"center": v(64.31, 45.08) * mm, "radius": 1.7 * mm});
            skCircle(sketch, "E384", {"center": v(51.05, 4.87) * mm, "radius": 1.7 * mm});
            skSolve(sketch);
        }
        {
            var Q0;
            Q0 = qSketchRegion(id + "F28", true);
            extrude(context, id + "F29", {"entities" : qUnion([Q0]), "depth" : 38 * mm, "offsetDistance" : 25 * mm});
        }
    });
